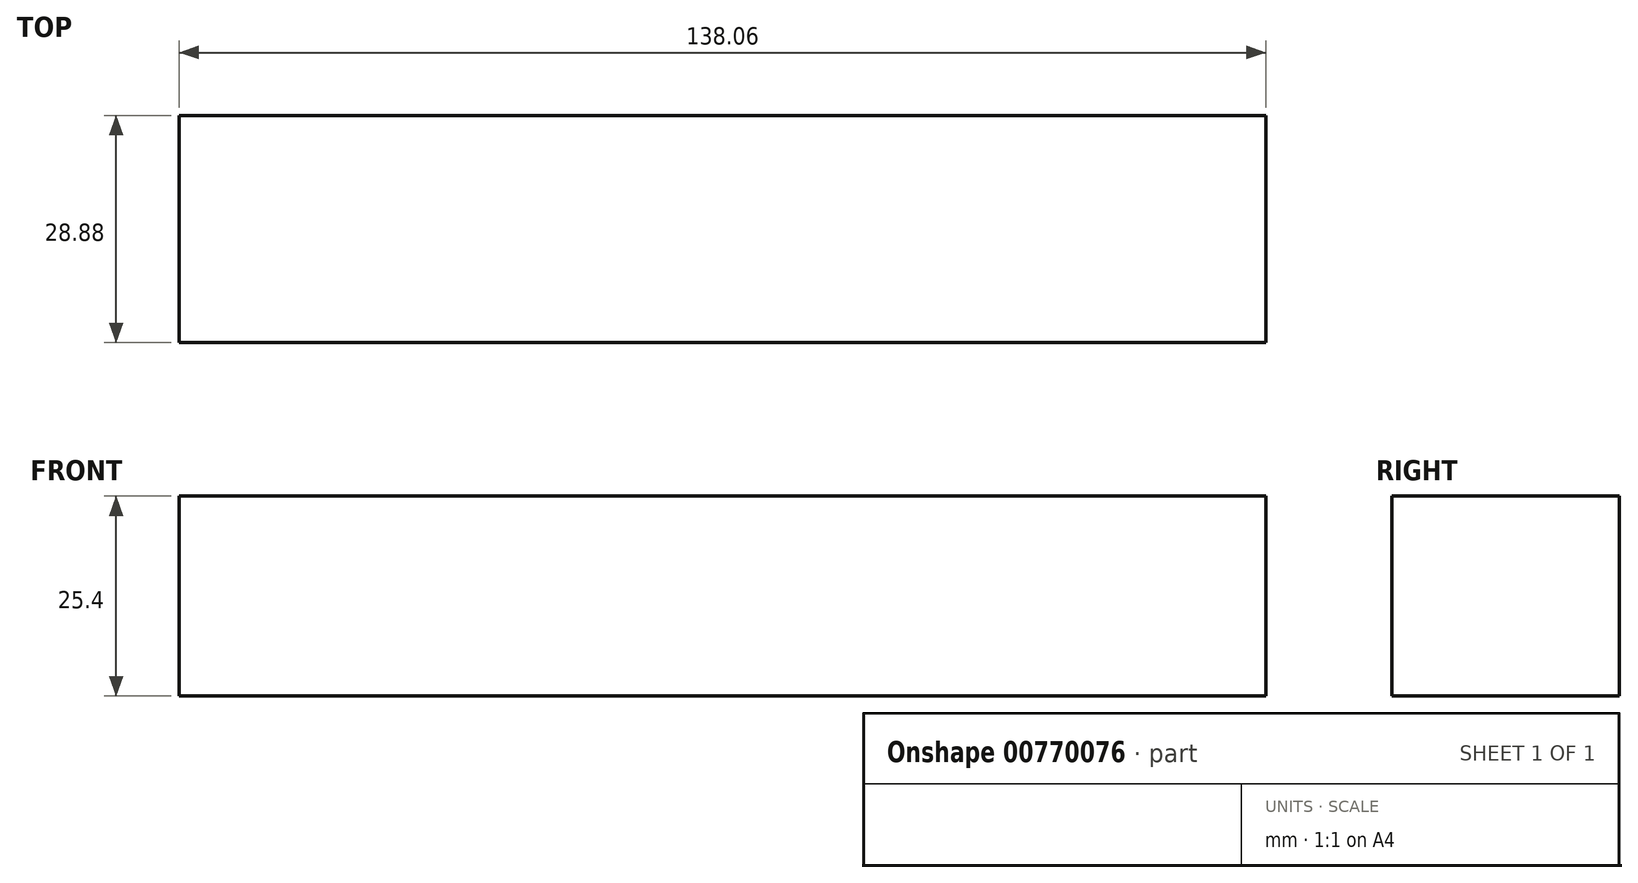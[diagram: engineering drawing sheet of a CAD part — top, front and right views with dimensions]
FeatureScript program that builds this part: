
annotation { "Feature Type Name" : "Feature", "Feature Type Description" : "" }
export const myFeature = defineFeature(function(context is Context, id is Id, definition is map)
    precondition{}
    {
        {
            var Q0;
            Q0=qCreatedBy(makeId("Top.planeOp"),FACE);
            var sketch = newSketch(context, id + "F0", { "sketchPlane" : qUnion([Q0])});
            skLineSegment(sketch, "E0.bottom", {"start": v(59.62, 47.67) * mm, "end": v(-78.44, 47.67) * mm});
            skLineSegment(sketch, "E0.top", {"start": v(59.62, 76.55) * mm, "end": v(-78.44, 76.55) * mm});
            skLineSegment(sketch, "E0.left", {"start": v(59.62, 47.67) * mm, "end": v(59.62, 76.55) * mm});
            skLineSegment(sketch, "E0.right", {"start": v(-78.44, 47.67) * mm, "end": v(-78.44, 76.55) * mm});
            skSolve(sketch);
        }
        {
            var Q0;
            Q0 = qSketchRegion(id + "F0", true);
            var Q1;
            Q1=makeQuery(id+"F0.imprint","IMPRINT",FACE,{"disambiguationData":[TD([[makeQuery(id+"F0.imprint","IMPRINT",EDGE,{"derivedFrom":sQuery(id+"F0.wireOp",EDGE,"E0.bottom")}),-1.0]])]});
            extrude(context, id + "F1", {"entities" : qUnion([Q0, Q1]), "depth" : 25.4 * mm, "offsetDistance" : 25.4 * mm});
        }
    });
